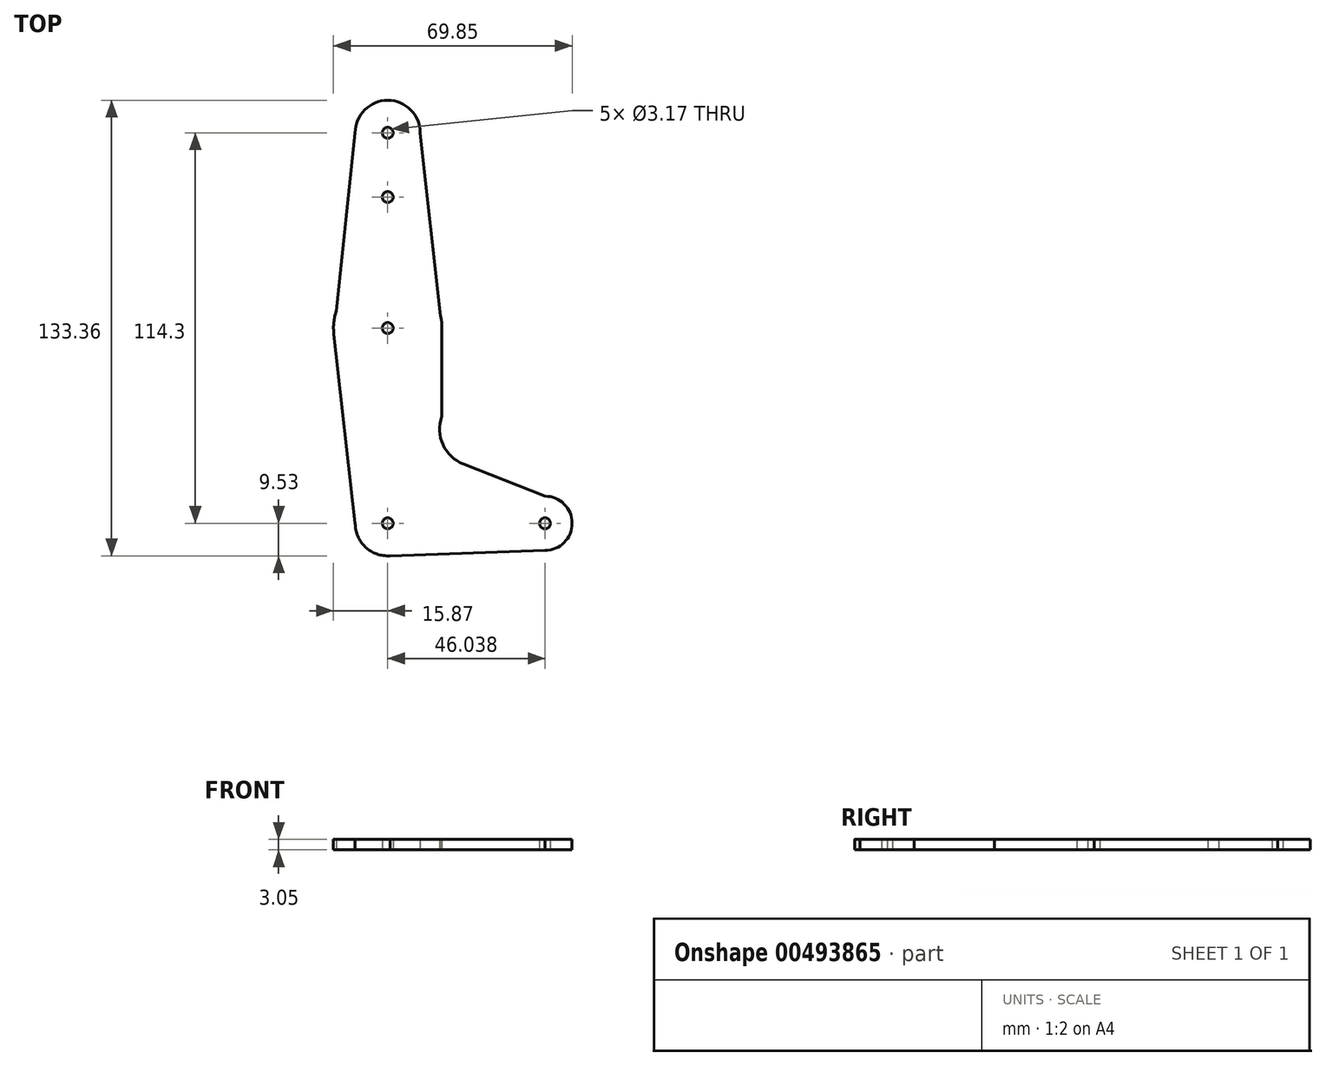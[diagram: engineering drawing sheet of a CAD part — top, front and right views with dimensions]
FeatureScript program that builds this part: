
annotation { "Feature Type Name" : "Feature", "Feature Type Description" : "" }
export const myFeature = defineFeature(function(context is Context, id is Id, definition is map)
    precondition{}
    {
        {
            var Q0;
            Q0=qCreatedBy(makeId("Top.planeOp"),FACE);
            var sketch = newSketch(context, id + "F0", { "sketchPlane" : qUnion([Q0])});
            skLineSegment(sketch, "E0", {"start": v(0, 0) * mm, "end": v(0, 114.3) * mm});
            skLineSegment(sketch, "E1", {"start": v(0, 0) * mm, "end": v(0, 0) * mm});
            skCircle(sketch, "E2", {"center": v(0, 114.3) * mm, "radius": 9.53 * mm});
            skCircle(sketch, "E3", {"center": v(0, 0) * mm, "radius": 9.53 * mm});
            skCircle(sketch, "E4", {"center": v(46.04, 0) * mm, "radius": 7.94 * mm});
            skCircle(sketch, "E5", {"center": v(0, 57.15) * mm, "radius": 15.88 * mm});
            skLineSegment(sketch, "E6", {"start": v(-9.52, 0) * mm, "end": v(-15.77, 55.37) * mm});
            skLineSegment(sketch, "E7", {"start": v(-15.77, 55.37) * mm, "end": v(-9.53, 114.3) * mm});
            skLineSegment(sketch, "E8", {"start": v(0, -9.52) * mm, "end": v(46.04, -7.94) * mm});
            skCircle(sketch, "E9", {"center": v(0, 114.3) * mm, "radius": 1.59 * mm});
            skCircle(sketch, "E10", {"center": v(0, 95.5) * mm, "radius": 1.59 * mm});
            skCircle(sketch, "E11", {"center": v(0, 57.15) * mm, "radius": 1.59 * mm});
            skCircle(sketch, "E12", {"center": v(0, 0) * mm, "radius": 1.59 * mm});
            skCircle(sketch, "E13", {"center": v(46.04, 0) * mm, "radius": 1.59 * mm});
            skLineSegment(sketch, "E14", {"start": v(9.53, 114.3) * mm, "end": v(15.88, 57.15) * mm});
            skLineSegment(sketch, "E15", {"start": v(22.19, 17.32) * mm, "end": v(46.04, 7.94) * mm});
            skLineSegment(sketch, "E16", {"start": v(15.87, 57.15) * mm, "end": v(15.83, 31.36) * mm});
            skArc(sketch, "E17", {"start": v(15.83, 31.36) * mm, "mid": v(16.16, 23.05) * mm, "end": v(22.19, 17.32) * mm});
            skLineSegment(sketch, "E18", {"start": v(9.52, 0) * mm, "end": v(46.04, 0) * mm});
            skSolve(sketch);
        }
        {
            var Q0;
            Q0 = qSketchRegion(id + "F0", true);
            extrude(context, id + "F1", {"entities" : qUnion([Q0]), "depth" : 3.05 * mm, "offsetDistance" : 25.4 * mm});
        }
    });
